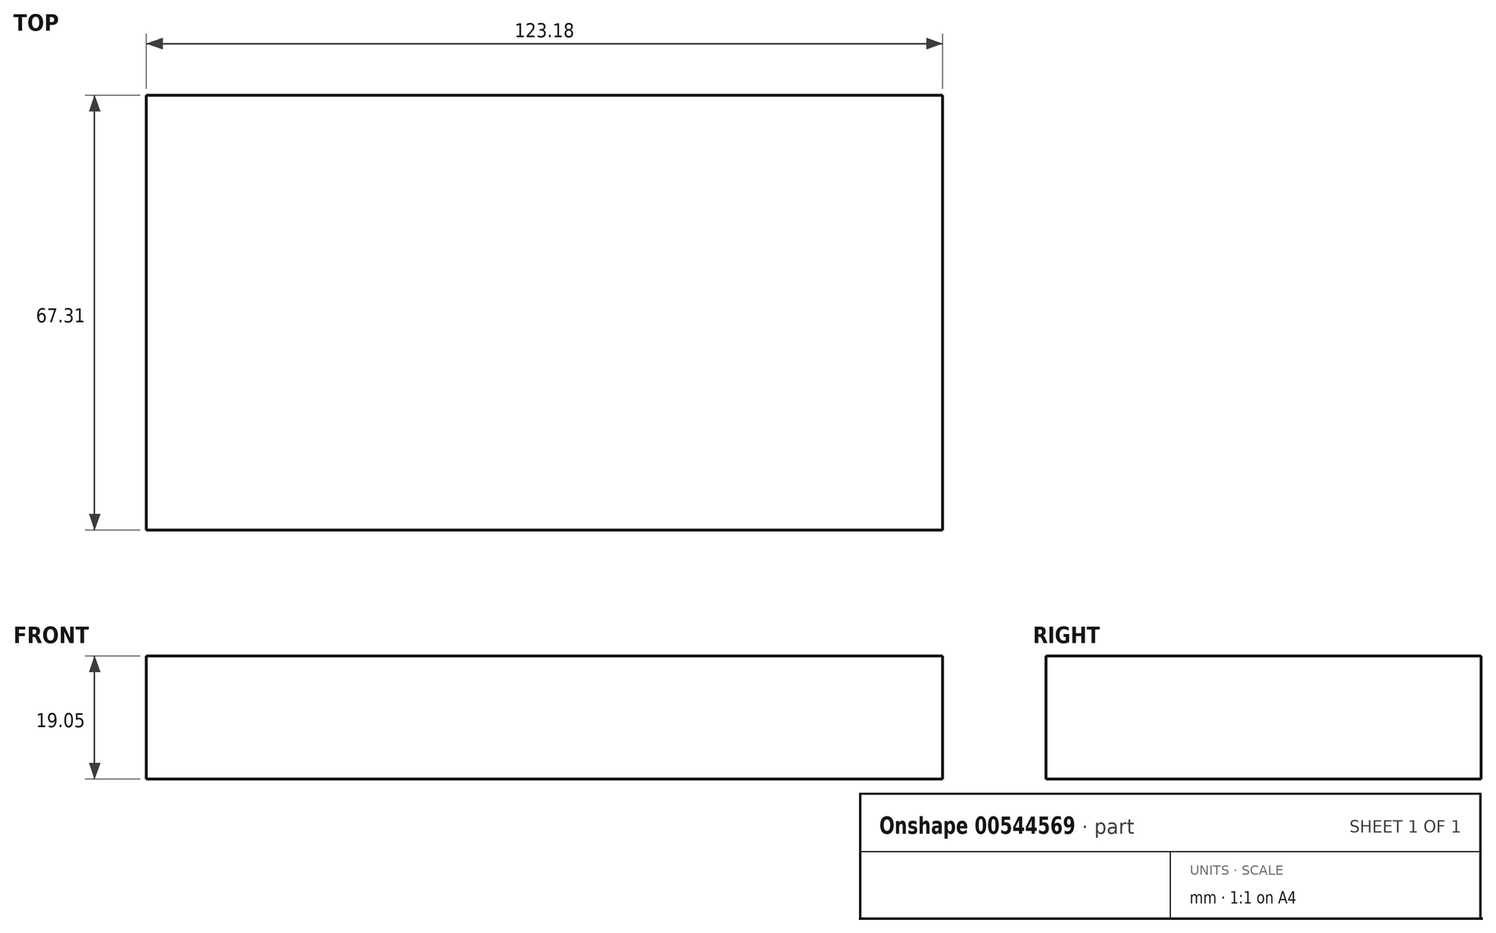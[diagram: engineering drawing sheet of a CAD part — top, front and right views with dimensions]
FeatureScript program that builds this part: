
annotation { "Feature Type Name" : "Feature", "Feature Type Description" : "" }
export const myFeature = defineFeature(function(context is Context, id is Id, definition is map)
    precondition{}
    {
        {
            var Q0;
            Q0=qCreatedBy(makeId("Top.planeOp"),FACE);
            var sketch = newSketch(context, id + "F0", { "sketchPlane" : qUnion([Q0])});
            skLineSegment(sketch, "E0", {"start": v(-75.8, 0) * mm, "end": v(-198.97, 0) * mm});
            skLineSegment(sketch, "E1", {"start": v(-198.97, 0) * mm, "end": v(-198.97, 67.34) * mm});
            skLineSegment(sketch, "E2", {"start": v(-198.97, 67.34) * mm, "end": v(-75.8, 67.34) * mm});
            skLineSegment(sketch, "E3", {"start": v(-75.8, 0) * mm, "end": v(-75.8, 67.34) * mm});
            skSolve(sketch);
        }
        {
            var Q0;
            Q0=makeQuery(id+"F0.imprint","IMPRINT",FACE,{"disambiguationData":[TD([[makeQuery(id+"F0.imprint","IMPRINT",EDGE,{"derivedFrom":sQuery(id+"F0.wireOp",EDGE,"E0")}),-1.0]])]});
            var Q1;
            Q1 = qConstructionFilter(qBodyType(qCreatedBy(id + "F0" ,EDGE), BodyType.WIRE), ConstructionObject.NO);
            extrude(context, id + "F1", {"entities" : qUnion([Q0]), "bodyType" : ToolBodyType.SURFACE, "operationType" : NewBodyOperationType.REMOVE, "surfaceEntities" : qUnion([Q1]), "depth" : 44.45 * mm, "offsetDistance" : 25.4 * mm, "hasSecondDirection" : true, "secondDirectionOppositeDirection" : false, "secondDirectionDepth" : 25.4 * mm});
        }
        {
            var Q0;
            Q0=makeQuery(id+"F1.opExtrude","SWEPT_FACE",FACE,{"disambiguationData":[OSD([sQuery(id+"F0.wireOp",EDGE,"E2")])]});
            extrude(context, id + "F2", {"entities" : qUnion([Q0]), "depth" : 67.3 * mm, "offsetDistance" : 25.4 * mm});
        }
    });
